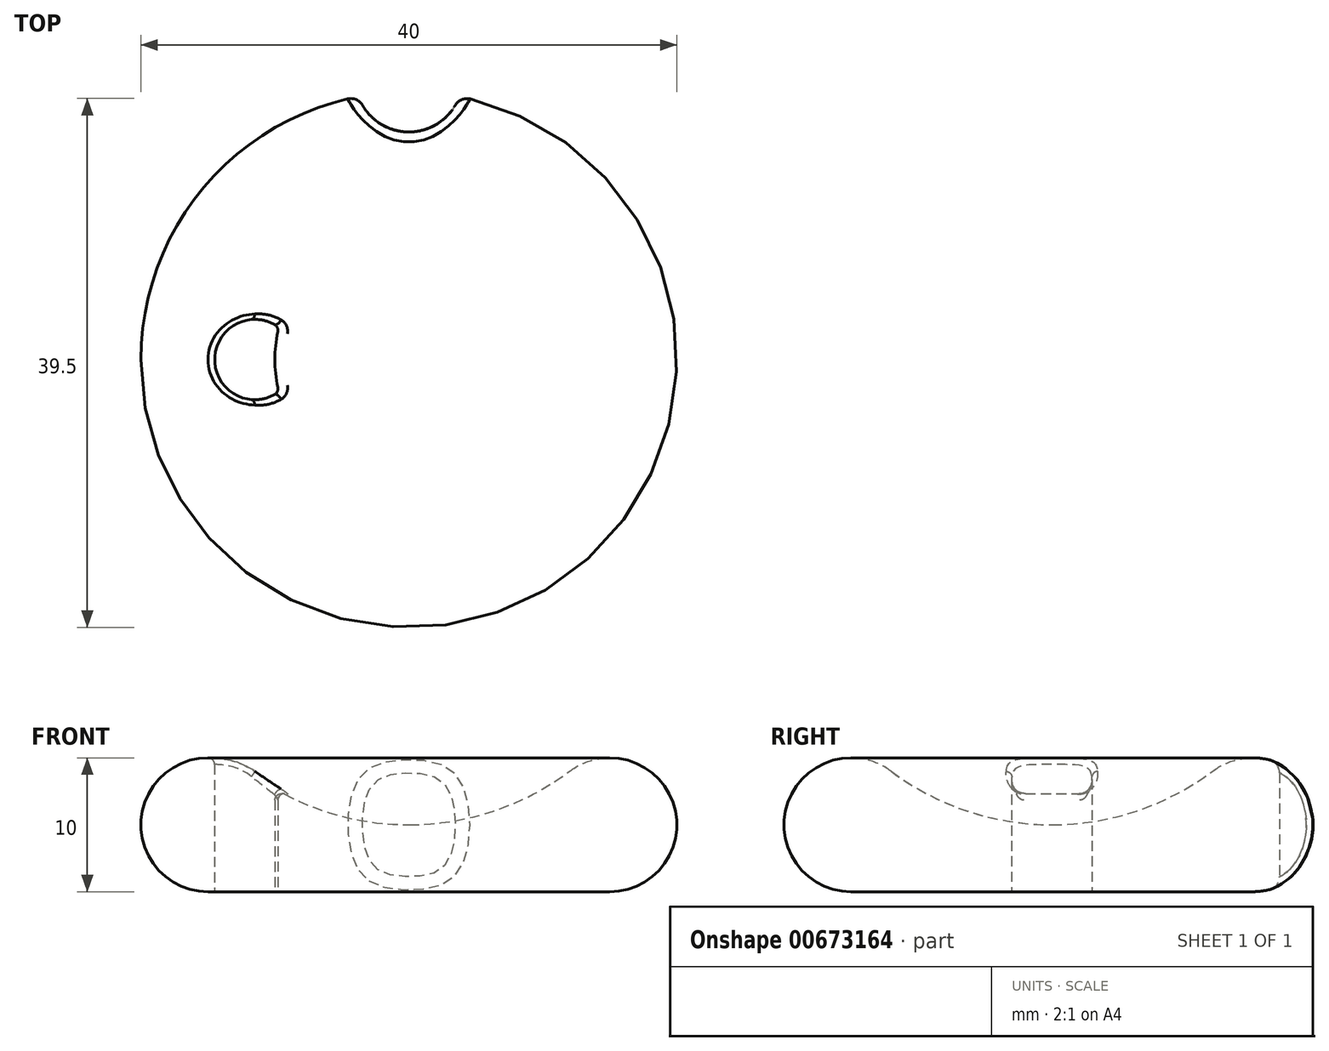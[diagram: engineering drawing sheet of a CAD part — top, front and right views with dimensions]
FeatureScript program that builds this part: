
annotation { "Feature Type Name" : "Feature", "Feature Type Description" : "" }
export const myFeature = defineFeature(function(context is Context, id is Id, definition is map)
    precondition{}
    {
        {
            var Q0;
            Q0=qCreatedBy(makeId("Right.planeOp"),FACE);
            var sketch = newSketch(context, id + "F0", { "sketchPlane" : qUnion([Q0])});
            skArc(sketch, "E0", {"start": v(-12, 9) * mm, "mid": v(-19.74, 6.58) * mm, "end": v(-15, 0) * mm});
            skArc(sketch, "E1", {"start": v(-12, 9) * mm, "mid": v(-6.32, 6.03) * mm, "end": v(0, 5) * mm});
            skLineSegment(sketch, "E2", {"start": v(0, 0) * mm, "end": v(-15, 0) * mm});
            skLineSegment(sketch, "E3", {"start": v(0, 0) * mm, "end": v(0, 5) * mm});
            skSolve(sketch);
        }
        {
            var Q0;
            Q0 = qSketchRegion(id + "F0", true);
            var Q1;
            Q1=sQuery(id+"F0.wireOp",EDGE,"E3");
            revolve(context, id + "F1", {"entities" : qUnion([Q0]), "axis" : qUnion([Q1]), "revolveType" : RevolveType.FULL});
        }
        {
            var Q0;
            Q0=qCreatedBy(makeId("Top.planeOp"),FACE);
            var sketch = newSketch(context, id + "F2", { "sketchPlane" : qUnion([Q0])});
            skCircle(sketch, "E4", {"center": v(0, 21) * mm, "radius": 4 * mm});
            skSolve(sketch);
        }
        {
            var Q0;
            Q0=makeQuery(id+"F2.imprint","IMPRINT",FACE,{"disambiguationData":[TD([[makeQuery(id+"F2.imprint","IMPRINT",EDGE,{"derivedFrom":sQuery(id+"F2.wireOp",EDGE,"E4")}),1.0]])]});
            extrude(context, id + "F3", {"entities" : qUnion([Q0]), "operationType" : NewBodyOperationType.REMOVE, "depth" : 25 * mm, "offsetDistance" : 25 * mm});
        }
        {
            var Q0;
            Q0=makeQuery(id+"F3.boolean.opBoolean","INTERSECT",EDGE,{"derivedFrom":[makeQuery(id+"F1.opRevolve","SWEPT_FACE",FACE,{"disambiguationData":[OSD([sQuery(id+"F0.wireOp",EDGE,"E0")])]}),makeQuery(id+"F3.opExtrude","SWEPT_FACE",FACE,{"disambiguationData":[OSD([sQuery(id+"F2.wireOp",EDGE,"E4")])]})]});
            fillet(context, id + "F4", {"entities" : qUnion([Q0]), "radius" : 1 * mm, "tangentPropagation" : true, "allowEdgeOverflow" : false});
        }
        {
            var Q0;
            Q0=qCreatedBy(makeId("Top.planeOp"),FACE);
            var sketch = newSketch(context, id + "F5", { "sketchPlane" : qUnion([Q0])});
            skCircle(sketch, "E5", {"center": v(-11.5, 0) * mm, "radius": 3 * mm});
            skCircle(sketch, "E6.0", {"center": v(0, 0) * mm, "radius": 10 * mm});
            skSolve(sketch);
        }
        {
            var Q0;
            {var subQ0=sQuery(id+"F5.wireOp",EDGE,"E6.0");var subQ1=sQuery(id+"F5.wireOp",EDGE,"E5");var subQ2=makeQuery(id+"F5.imprint","INTERSECT",VERTEX,{"disambiguationData":[OD(0.0)],"derivedFrom":[subQ1,subQ0]});Q0=makeQuery(id+"F5.imprint","IMPRINT",FACE,{"disambiguationData":[TD([[makeQuery(id+"F5.imprint","IMPRINT",EDGE,{"disambiguationData":[TD([[subQ2,1.0]])],"derivedFrom":subQ1}),1.0]])]});}
            extrude(context, id + "F6", {"entities" : qUnion([Q0]), "operationType" : NewBodyOperationType.REMOVE, "depth" : 25 * mm, "offsetDistance" : 25 * mm});
        }
        {
            var Q0;
            {var subQ0=sQuery(id+"F5.wireOp",EDGE,"E6.0");var subQ1=sQuery(id+"F5.wireOp",EDGE,"E5");Q0=makeQuery(id+"F6.boolean.opBoolean","COPY",EDGE,{"derivedFrom":makeQuery(id+"F6.opExtrude","SWEPT_EDGE",EDGE,{"disambiguationData":[OSD([subQ1,subQ0]),TDD([makeQuery(id+"F5.imprint","INTERSECT",VERTEX,{"disambiguationData":[OD(1.0)],"derivedFrom":[subQ1,subQ0]})])]})});}
            var Q1;
            {var subQ0=sQuery(id+"F5.wireOp",EDGE,"E6.0");var subQ1=sQuery(id+"F5.wireOp",EDGE,"E5");Q1=makeQuery(id+"F6.boolean.opBoolean","COPY",EDGE,{"derivedFrom":makeQuery(id+"F6.opExtrude","SWEPT_EDGE",EDGE,{"disambiguationData":[OSD([subQ1,subQ0]),TDD([makeQuery(id+"F5.imprint","INTERSECT",VERTEX,{"disambiguationData":[OD(0.0)],"derivedFrom":[subQ1,subQ0]})])]})});}
            var Q2;
            Q2=makeQuery(id+"F6.boolean.opBoolean","INTERSECT",EDGE,{"derivedFrom":[makeQuery(id+"F1.opRevolve","SWEPT_FACE",FACE,{"disambiguationData":[OSD([sQuery(id+"F0.wireOp",EDGE,"E1")])]}),makeQuery(id+"F6.opExtrude","SWEPT_FACE",FACE,{"disambiguationData":[OSD([sQuery(id+"F5.wireOp",EDGE,"E6.0")])]})]});
            var Q3;
            Q3=makeQuery(id+"F6.boolean.opBoolean","INTERSECT",EDGE,{"derivedFrom":[makeQuery(id+"F1.opRevolve","SWEPT_FACE",FACE,{"disambiguationData":[OSD([sQuery(id+"F0.wireOp",EDGE,"E0")])]}),makeQuery(id+"F6.opExtrude","SWEPT_FACE",FACE,{"disambiguationData":[OSD([sQuery(id+"F5.wireOp",EDGE,"E5")])]})]});
            var Q4;
            Q4=makeQuery(id+"F6.boolean.opBoolean","INTERSECT",EDGE,{"disambiguationData":[OD(1.0)],"derivedFrom":[makeQuery(id+"F1.opRevolve","SWEPT_FACE",FACE,{"disambiguationData":[OSD([sQuery(id+"F0.wireOp",EDGE,"E1")])]}),makeQuery(id+"F6.opExtrude","SWEPT_FACE",FACE,{"disambiguationData":[OSD([sQuery(id+"F5.wireOp",EDGE,"E5")])]})]});
            var Q5;
            Q5=makeQuery(id+"F6.boolean.opBoolean","COPY",EDGE,{"derivedFrom":makeQuery(id+"F6.opExtrude","CAP_EDGE",EDGE,{"disambiguationData":[OSD([sQuery(id+"F5.wireOp",EDGE,"E5")])],"isStart":true})});
            var Q6;
            Q6=makeQuery(id+"F6.boolean.opBoolean","COPY",EDGE,{"derivedFrom":makeQuery(id+"F6.opExtrude","CAP_EDGE",EDGE,{"disambiguationData":[OSD([sQuery(id+"F5.wireOp",EDGE,"E6.0")])],"isStart":true})});
            fillet(context, id + "F7", {"entities" : qUnion([Q0, Q1, Q2, Q3, Q4, Q5, Q6]), "radius" : 0.5 * mm, "tangentPropagation" : true, "allowEdgeOverflow" : false});
        }
    });
